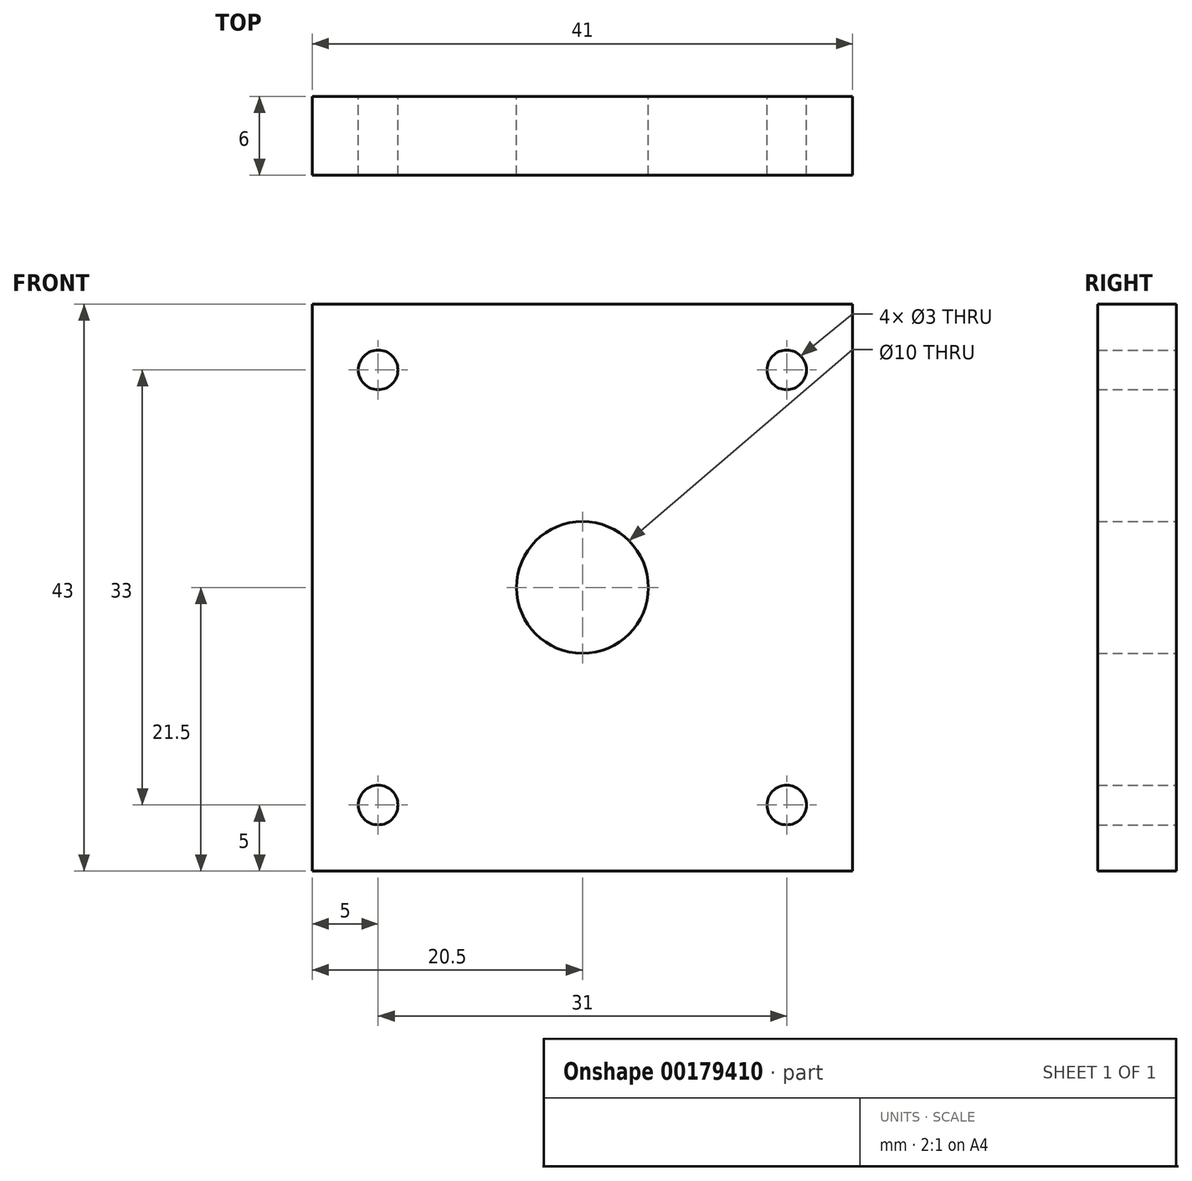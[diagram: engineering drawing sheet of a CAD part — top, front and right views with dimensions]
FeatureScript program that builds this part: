
annotation { "Feature Type Name" : "Feature", "Feature Type Description" : "" }
export const myFeature = defineFeature(function(context is Context, id is Id, definition is map)
    precondition{}
    {
        {
            var Q0;
            Q0=qCreatedBy(makeId("Front.planeOp"),FACE);
            var sketch = newSketch(context, id + "F0", { "sketchPlane" : qUnion([Q0])});
            skLineSegment(sketch, "E0.bottom", {"start": v(-20.5, -21.5) * mm, "end": v(20.5, -21.5) * mm});
            skLineSegment(sketch, "E0.top", {"start": v(-20.5, 21.5) * mm, "end": v(20.5, 21.5) * mm});
            skLineSegment(sketch, "E0.left", {"start": v(-20.5, -21.5) * mm, "end": v(-20.5, 21.5) * mm});
            skLineSegment(sketch, "E0.right", {"start": v(20.5, -21.5) * mm, "end": v(20.5, 21.5) * mm});
            skPoint(sketch, "E0.middle", {"position": v(0, 0) * mm});
            skCircle(sketch, "E1", {"center": v(-15.5, 16.5) * mm, "radius": 1.5 * mm});
            skLineSegment(sketch, "E2", {"start": v(-20.5, 0) * mm, "end": v(20.5, 0) * mm, "construction": true});
            skLineSegment(sketch, "E3", {"start": v(0, 21.5) * mm, "end": v(0, -21.5) * mm, "construction": true});
            skCircle(sketch, "E4.MirrorC", {"center": v(15.5, 16.5) * mm, "radius": 1.5 * mm});
            skCircle(sketch, "E5.MirrorC", {"center": v(-15.5, -16.5) * mm, "radius": 1.5 * mm});
            skCircle(sketch, "E6.MirrorC", {"center": v(15.5, -16.5) * mm, "radius": 1.5 * mm});
            skCircle(sketch, "E7", {"center": v(0, 0) * mm, "radius": 5 * mm});
            skSolve(sketch);
        }
        {
            var Q0;
            Q0 = qSketchRegion(id + "F0", true);
            extrude(context, id + "F1", {"entities" : qUnion([Q0]), "depth" : 6 * mm});
        }
    });
